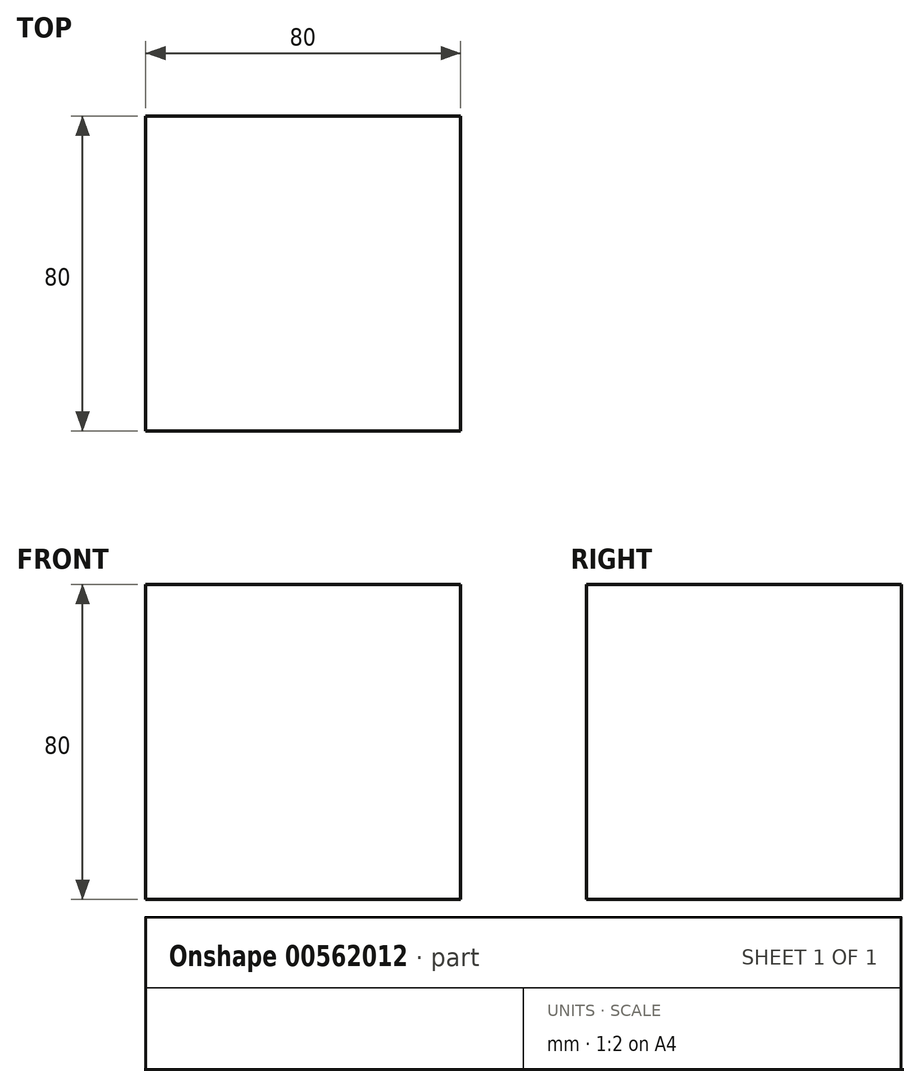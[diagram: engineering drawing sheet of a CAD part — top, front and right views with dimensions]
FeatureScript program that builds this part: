
annotation { "Feature Type Name" : "Feature", "Feature Type Description" : "" }
export const myFeature = defineFeature(function(context is Context, id is Id, definition is map)
    precondition{}
    {
        {
            var Q0;
            Q0=qCreatedBy(makeId("Top.planeOp"),FACE);
            var sketch = newSketch(context, id + "F0", { "sketchPlane" : qUnion([Q0])});
            skLineSegment(sketch, "E0.bottom", {"start": v(40, -40) * mm, "end": v(-40, -40) * mm});
            skLineSegment(sketch, "E0.top", {"start": v(40, 40) * mm, "end": v(-40, 40) * mm});
            skLineSegment(sketch, "E0.left", {"start": v(40, -40) * mm, "end": v(40, 40) * mm});
            skLineSegment(sketch, "E0.right", {"start": v(-40, -40) * mm, "end": v(-40, 40) * mm});
            skPoint(sketch, "E0.middle", {"position": v(0, 0) * mm});
            skSolve(sketch);
        }
        {
            var Q0;
            Q0 = qSketchRegion(id + "F0", true);
            extrude(context, id + "F1", {"entities" : qUnion([Q0]), "depth" : 80 * mm, "offsetDistance" : 25 * mm});
        }
    });
